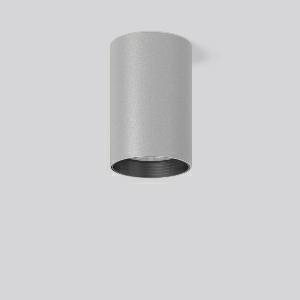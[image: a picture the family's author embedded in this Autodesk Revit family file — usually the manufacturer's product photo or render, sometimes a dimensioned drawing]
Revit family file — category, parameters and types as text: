
# Revit family: heledon_maxi_a_931229_004_2_e8a2
name_source: partatom
category: Lighting Fixtures
units: mm (PartAtom-declared; Revit-internal decimal feet)

## family parameters
Cut with Voids When Loaded = No
Host = Face
Light Source = No
Part Type = Normal
Room Calculation Point = No
Round Connector Dimension = Use Diameter
Shared = No

## types (1)
- HELEDON maxi A (1 x LED Modul 927, 3450 lm, 2700)
    Apparent Load = 35 VA
    Approval mark = CE
    CIE Flux Codes = 96 100 100 100 100
    Color Rendering = 92
    Color Temperature = 2700
    Default Elevation = 1800 mm
    Description = Series: HELEDON maxi
Cylindrical surface-mounted downlight. Housing: die-cast aluminium, powder-coated. Internal ceiling frame polycarbonate with bayonet mounting. Black plastic ring and recessed LED to prevent glare from the side. Optical assembly with lens made of plastic (polycarbonate) for the best homogeneous light distribution - can be changed without tools. Best colour rendering index Ra>90. Suitable for Ceiling mounting. Easy installation with a separate ceiling frame with bayonet mounting and plug connection. Driver integrated. Connected via plug-in connector. High quality converter without flickering and stroboscopic effect. The following accessories can be mounted without use of tools: interchangeable lenses, decorative glasses, honeycomb louvre, clear and frosted diffusers, white interchangeable plastic ring. 
Colour: silver
Diameter: 123 mm
Height: 183 mm
Lamp: LED
Socket: without socket
Colour temperature: 2700K
Colour rendering index (CRI): 92
System power: 35 W
Rated luminous flux: 3450 lm
Luminous efficiency: 99 lm/W
Control gear: Regulated power supply
Protection class: I
Type of protection: IP 20
    Height = 183 mm
    Lamp = 1 x LED Modul 927
    Lamp Light Flux = 3450 lm
    Lamp count = 1
    Length = 123 mm
    Lifetime = 50000 h
    Luminous efficacy = 99 lm/W
    Manufacturer = RZB
    ModVariant = No
    Model = 931229.004.2
    Mounting Place = Ceiling
    Mounting Type = Surface mounted
    Number of Poles = 1
    OnlyDefault = Yes
    Power Factor = 1
    Product Name = HELEDON maxi A
    Product group = Surface mounted downlights
    ProductGroupID = 302
    Protection Class = Protection class I
    Protection Degree = IP 20
    RLX_Detail_Level = 1
    RLX_Emergency_Light_Flux = 0 lm
    RLX_Emergency_Type = 0
    RLX_Emergency_Type_DB = No
    RlxData = <blob elided: 98369 chars, md5=b9a2e521>
    Socket = socket
    Standby Power = 0 W
    System Light Flux = 3450 lm
    System Power = 35 W
    Type Comments = Product without accessories
    Type Image = 931193.004.jpg
    URL = http://relux.com
    VarID = ---
    Voltage = 230 V
    Voltage Range = 220-240 V
    Weight = 0.00 kg
    Width = 0 mm  [stored 0 ft]

note: [stored X ft] marks values corroborated as IEEE doubles in the binary element streams (Revit-internal decimal feet)

## geometry (parser evidence)
native form markers: Blend x4, Sweep x10
no freeform markers — native parametric forms only
